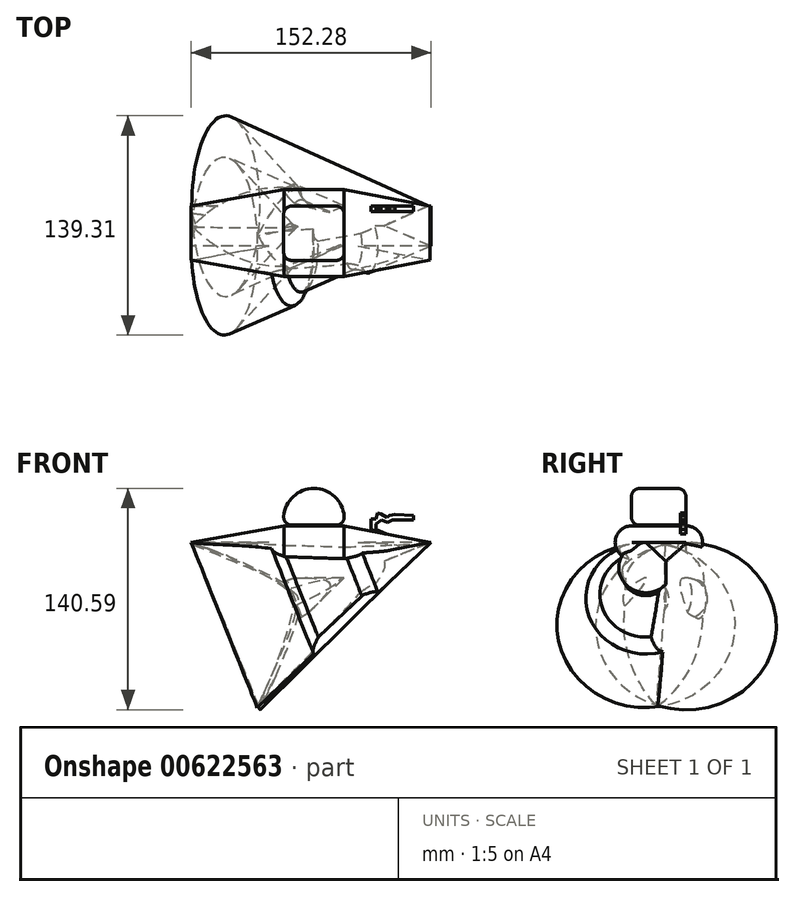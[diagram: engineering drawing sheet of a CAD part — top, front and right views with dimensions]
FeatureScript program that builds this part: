
annotation { "Feature Type Name" : "Feature", "Feature Type Description" : "" }
export const myFeature = defineFeature(function(context is Context, id is Id, definition is map)
    precondition{}
    {
        {
            var Q0;
            Q0=qCreatedBy(makeId("Front.planeOp"),FACE);
            var sketch = newSketch(context, id + "F0", { "sketchPlane" : qUnion([Q0])});
            skLineSegment(sketch, "E0", {"start": v(-76.05, 0) * mm, "end": v(-17.05, 10.6) * mm});
            skLineSegment(sketch, "E1", {"start": v(-17.05, 10.6) * mm, "end": v(21.1, 10.6) * mm});
            skLineSegment(sketch, "E2", {"start": v(21.1, 10.6) * mm, "end": v(75.68, 0) * mm});
            skLineSegment(sketch, "E3", {"start": v(75.68, 0) * mm, "end": v(-76.05, 0) * mm});
            skSolve(sketch);
        }
        {
            var Q0;
            Q0=makeQuery(id+"F0.imprint","IMPRINT",FACE,{"disambiguationData":[TD([[makeQuery(id+"F0.imprint","IMPRINT",EDGE,{"derivedFrom":sQuery(id+"F0.wireOp",EDGE,"E0")}),-1.0]])]});
            extrude(context, id + "F1", {"entities" : qUnion([Q0]), "depth" : 34.3 * mm, "offsetDistance" : 25.4 * mm});
        }
        {
            var Q0;
            Q0=makeQuery(id+"F1.opExtrude","CAP_FACE",FACE,{"disambiguationData":[OSD([sQuery(id+"F0.wireOp",EDGE,"E0"),sQuery(id+"F0.wireOp",EDGE,"E1"),sQuery(id+"F0.wireOp",EDGE,"E2"),sQuery(id+"F0.wireOp",EDGE,"E3")])],"isStart":false});
            var Q1;
            Q1=makeQuery(id+"F1.opExtrude","CAP_EDGE",EDGE,{"disambiguationData":[OSD([sQuery(id+"F0.wireOp",EDGE,"E3")])],"isStart":false});
            revolve(context, id + "F2", {"operationType" : NewBodyOperationType.ADD, "entities" : qUnion([Q0]), "axis" : qUnion([Q1]), "revolveType" : RevolveType.FULL});
        }
        {
            var Q0;
            Q0=makeQuery(id+"F1.opExtrude","CAP_FACE",FACE,{"disambiguationData":[OSD([sQuery(id+"F0.wireOp",EDGE,"E0"),sQuery(id+"F0.wireOp",EDGE,"E1"),sQuery(id+"F0.wireOp",EDGE,"E2"),sQuery(id+"F0.wireOp",EDGE,"E3")])],"isStart":true});
            var Q1;
            Q1=makeQuery(id+"F1.opExtrude","CAP_EDGE",EDGE,{"disambiguationData":[OSD([sQuery(id+"F0.wireOp",EDGE,"E3")])],"isStart":true});
            revolve(context, id + "F3", {"operationType" : NewBodyOperationType.ADD, "entities" : qUnion([Q0]), "axis" : qUnion([Q1]), "revolveType" : RevolveType.FULL});
        }
        {
            var Q0;
            Q0=qCreatedBy(makeId("Front.planeOp"),FACE);
            var sketch = newSketch(context, id + "F4", { "sketchPlane" : qUnion([Q0])});
            skArc(sketch, "E4", {"start": v(20.74, 10.97) * mm, "mid": v(1.94, 34.28) * mm, "end": v(-16.87, 10.97) * mm});
            skLineSegment(sketch, "E5", {"start": v(20.74, 10.97) * mm, "end": v(-16.87, 10.97) * mm});
            skSolve(sketch);
        }
        {
            var Q0;
            Q0=makeQuery(id+"F4.imprint","IMPRINT",FACE,{"disambiguationData":[TD([[makeQuery(id+"F4.imprint","IMPRINT",EDGE,{"derivedFrom":sQuery(id+"F4.wireOp",EDGE,"E4")}),1.0]])]});
            extrude(context, id + "F5", {"entities" : qUnion([Q0]), "depth" : 34.54 * mm, "offsetDistance" : 25.4 * mm});
        }
        {
            var Q0;
            Q0=makeQuery(id+"F5.opExtrude","SWEPT_FACE",FACE,{"disambiguationData":[OSD([sQuery(id+"F4.wireOp",EDGE,"E4")])]});
            var Q1;
            Q1=makeQuery(id+"F5.opExtrude","CAP_FACE",FACE,{"disambiguationData":[OSD([sQuery(id+"F4.wireOp",EDGE,"E4"),sQuery(id+"F4.wireOp",EDGE,"E5")])],"isStart":true});
            var Q2;
            Q2=makeQuery(id+"F5.opExtrude","CAP_FACE",FACE,{"disambiguationData":[OSD([sQuery(id+"F4.wireOp",EDGE,"E4"),sQuery(id+"F4.wireOp",EDGE,"E5")])],"isStart":false});
            fillet(context, id + "F6", {"entities" : qUnion([Q0, Q1, Q2]), "radius" : 5.08 * mm, "tangentPropagation" : true, "allowEdgeOverflow" : false});
        }
        {
            var Q0;
            Q0=qCreatedBy(makeId("Front.planeOp"),FACE);
            var sketch = newSketch(context, id + "F7", { "sketchPlane" : qUnion([Q0])});
            skLineSegment(sketch, "E6", {"start": v(-76.05, 0) * mm, "end": v(-18.34, -22.4) * mm});
            skLineSegment(sketch, "E7", {"start": v(-18.34, -22.4) * mm, "end": v(20.19, -22.4) * mm});
            skLineSegment(sketch, "E8", {"start": v(20.19, -22.4) * mm, "end": v(76.23, 0) * mm});
            skLineSegment(sketch, "E9", {"start": v(76.23, 0) * mm, "end": v(-76.05, 0) * mm});
            skSolve(sketch);
        }
        {
            var Q0;
            Q0=makeQuery(id+"F7.imprint","IMPRINT",FACE,{"disambiguationData":[TD([[makeQuery(id+"F7.imprint","IMPRINT",EDGE,{"derivedFrom":sQuery(id+"F7.wireOp",EDGE,"E6")}),1.0]])]});
            extrude(context, id + "F8", {"entities" : qUnion([Q0]), "operationType" : NewBodyOperationType.ADD, "depth" : 25.4 * mm, "offsetDistance" : 25.4 * mm});
        }
        {
            var Q0;
            Q0=makeQuery(id+"F8.opExtrude","CAP_FACE",FACE,{"disambiguationData":[OSD([sQuery(id+"F7.wireOp",EDGE,"E6"),sQuery(id+"F7.wireOp",EDGE,"E7"),sQuery(id+"F7.wireOp",EDGE,"E8"),sQuery(id+"F7.wireOp",EDGE,"E9")])],"isStart":false});
            var Q1;
            Q1=makeQuery(id+"F8.opExtrude","CAP_EDGE",EDGE,{"disambiguationData":[OSD([sQuery(id+"F7.wireOp",EDGE,"E8")])],"isStart":false});
            revolve(context, id + "F9", {"operationType" : NewBodyOperationType.ADD, "entities" : qUnion([Q0]), "axis" : qUnion([Q1]), "revolveType" : RevolveType.FULL});
        }
        {
            var Q0;
            Q0=qCreatedBy(makeId("Front.planeOp"),FACE);
            var sketch = newSketch(context, id + "F10", { "sketchPlane" : qUnion([Q0])});
            skLineSegment(sketch, "E10", {"start": v(76.39, 0) * mm, "end": v(20.94, -22.6) * mm});
            skLineSegment(sketch, "E11", {"start": v(20.94, -22.6) * mm, "end": v(-15.65, -22.6) * mm});
            skLineSegment(sketch, "E12", {"start": v(-15.65, -22.6) * mm, "end": v(-75.7, 0) * mm});
            skLineSegment(sketch, "E13", {"start": v(-75.7, 0) * mm, "end": v(74.65, -0.7) * mm});
            skSolve(sketch);
        }
        {
            var Q0;
            {var subQ0=sQuery(id+"F10.wireOp",EDGE,"E11");Q0=makeQuery(id+"F10.imprint","IMPRINT",FACE,{"disambiguationData":[TD([[makeQuery(id+"F10.imprint","IMPRINT",EDGE,{"derivedFrom":subQ0}),-1.0]])]});}
            var Q1;
            Q1=sQuery(id+"F10.wireOp",EDGE,"E10");
            revolve(context, id + "F11", {"operationType" : NewBodyOperationType.ADD, "entities" : qUnion([Q0]), "axis" : qUnion([Q1]), "revolveType" : RevolveType.FULL});
        }
        {
            var Q0;
            Q0=qCreatedBy(makeId("Front.planeOp"),FACE);
            var sketch = newSketch(context, id + "F12", { "sketchPlane" : qUnion([Q0])});
            skLineSegment(sketch, "E14", {"start": v(38.1, 8.24) * mm, "end": v(38.1, 15.08) * mm});
            skLineSegment(sketch, "E15", {"start": v(38.1, 15.08) * mm, "end": v(41.41, 15.08) * mm});
            skLineSegment(sketch, "E16", {"start": v(41.41, 15.08) * mm, "end": v(42.3, 18.84) * mm});
            skLineSegment(sketch, "E17", {"start": v(42.3, 18.84) * mm, "end": v(44.5, 17.95) * mm});
            skLineSegment(sketch, "E18", {"start": v(44.5, 17.95) * mm, "end": v(48.25, 15.74) * mm});
            skLineSegment(sketch, "E19", {"start": v(48.25, 15.74) * mm, "end": v(50.02, 17.3) * mm});
            skLineSegment(sketch, "E20", {"start": v(50.02, 17.3) * mm, "end": v(53.55, 17.73) * mm});
            skLineSegment(sketch, "E21", {"start": v(53.55, 17.73) * mm, "end": v(65.03, 17.07) * mm});
            skLineSegment(sketch, "E22", {"start": v(65.03, 17.07) * mm, "end": v(65.25, 14.2) * mm});
            skLineSegment(sketch, "E23", {"start": v(65.25, 14.2) * mm, "end": v(51.79, 14.2) * mm});
            skLineSegment(sketch, "E24", {"start": v(51.79, 14.2) * mm, "end": v(48.48, 12.65) * mm});
            skLineSegment(sketch, "E25", {"start": v(48.48, 12.65) * mm, "end": v(44.94, 14.2) * mm});
            skLineSegment(sketch, "E26", {"start": v(44.94, 14.2) * mm, "end": v(41.41, 11.66) * mm});
            skPoint(sketch, "E26.endSnap0", {"position": v(38.1, 11.66) * mm});
            skLineSegment(sketch, "E27", {"start": v(41.41, 11.66) * mm, "end": v(38.1, 8.24) * mm});
            skLineSegment(sketch, "E28", {"start": v(41.41, 11.66) * mm, "end": v(41.41, 8.24) * mm});
            skLineSegment(sketch, "E29", {"start": v(41.41, 8.24) * mm, "end": v(48.48, 5.15) * mm});
            skLineSegment(sketch, "E30", {"start": v(48.48, 5.15) * mm, "end": v(38.1, 8.24) * mm});
            skSolve(sketch);
        }
        {
            var Q0;
            Q0=makeQuery(id+"F12.imprint","IMPRINT",FACE,{"disambiguationData":[TD([[makeQuery(id+"F12.imprint","IMPRINT",EDGE,{"derivedFrom":sQuery(id+"F12.wireOp",EDGE,"E27")}),1.0]])]});
            var Q1;
            Q1=makeQuery(id+"F12.imprint","IMPRINT",FACE,{"disambiguationData":[TD([[makeQuery(id+"F12.imprint","IMPRINT",EDGE,{"derivedFrom":sQuery(id+"F12.wireOp",EDGE,"E14")}),-1.0]])]});
            extrude(context, id + "F13", {"entities" : qUnion([Q0, Q1]), "operationType" : NewBodyOperationType.ADD, "depth" : 3.56 * mm, "offsetDistance" : 25.4 * mm});
        }
    });
